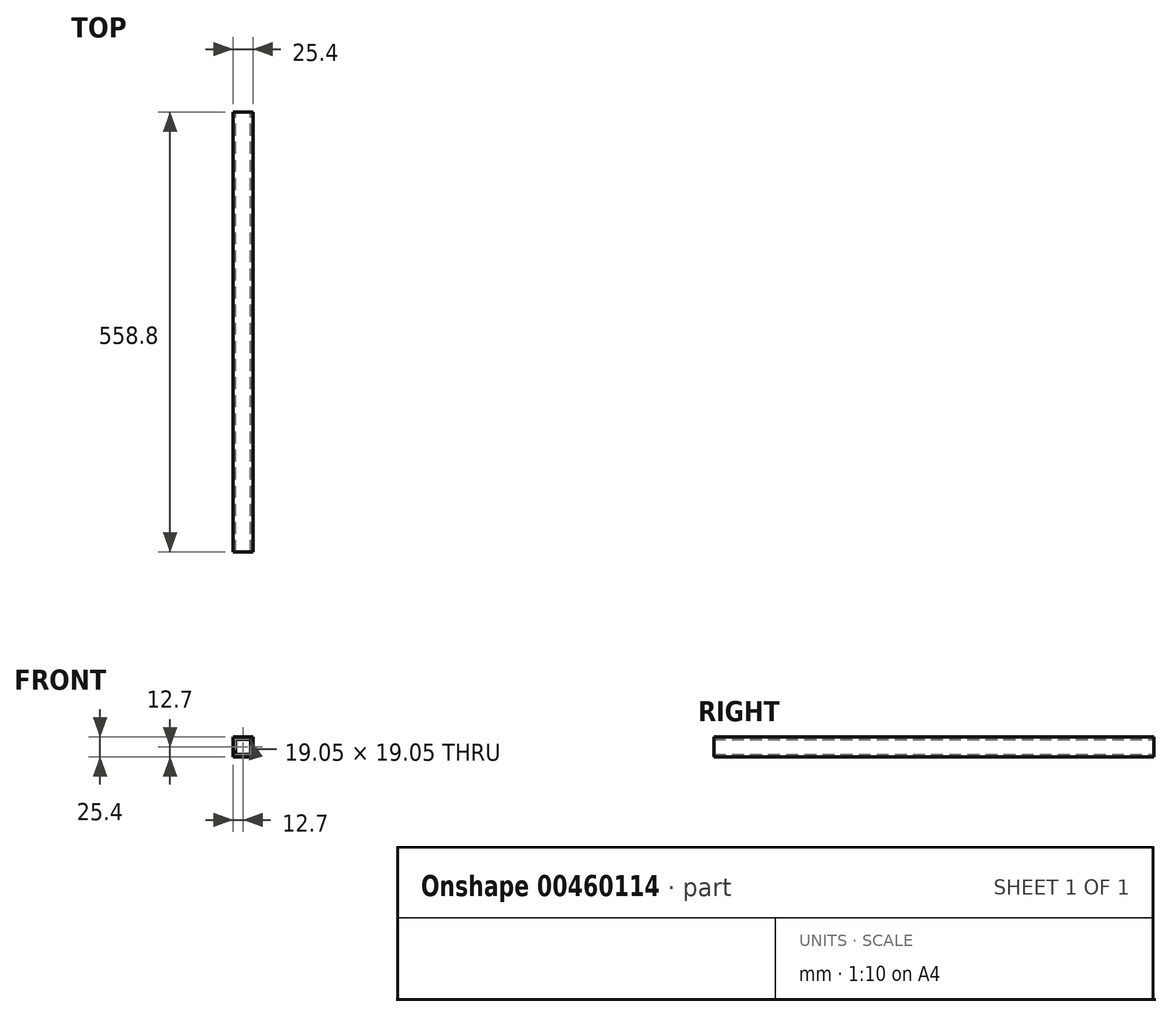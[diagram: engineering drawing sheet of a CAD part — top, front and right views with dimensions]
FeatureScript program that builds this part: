
annotation { "Feature Type Name" : "Feature", "Feature Type Description" : "" }
export const myFeature = defineFeature(function(context is Context, id is Id, definition is map)
    precondition{}
    {
        {
            var Q0;
            Q0=qCreatedBy(makeId("Front.planeOp"),FACE);
            var sketch = newSketch(context, id + "F0", { "sketchPlane" : qUnion([Q0])});
            skLineSegment(sketch, "E0.bottom", {"start": v(0, 0) * mm, "end": v(25.4, 0) * mm});
            skLineSegment(sketch, "E0.top", {"start": v(0, 25.4) * mm, "end": v(25.4, 25.4) * mm});
            skLineSegment(sketch, "E0.left", {"start": v(0, 0) * mm, "end": v(0, 25.4) * mm});
            skLineSegment(sketch, "E0.right", {"start": v(25.4, 0) * mm, "end": v(25.4, 25.4) * mm});
            skLineSegment(sketch, "E1.bottom", {"start": v(3.17, 3.18) * mm, "end": v(22.22, 3.18) * mm});
            skLineSegment(sketch, "E1.top", {"start": v(3.17, 22.22) * mm, "end": v(22.22, 22.22) * mm});
            skLineSegment(sketch, "E1.left", {"start": v(3.17, 3.18) * mm, "end": v(3.17, 22.22) * mm});
            skLineSegment(sketch, "E1.right", {"start": v(22.22, 3.18) * mm, "end": v(22.22, 22.22) * mm});
            skSolve(sketch);
        }
        {
            var Q0;
            Q0=makeQuery(id+"F0.imprint","IMPRINT",FACE,{"disambiguationData":[TD([[makeQuery(id+"F0.imprint","IMPRINT",EDGE,{"derivedFrom":sQuery(id+"F0.wireOp",EDGE,"E0.bottom")}),1.0]])]});
            extrude(context, id + "F1", {"entities" : qUnion([Q0]), "depth" : 558.8 * mm, "offsetDistance" : 25.4 * mm});
        }
    });
